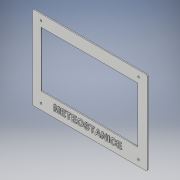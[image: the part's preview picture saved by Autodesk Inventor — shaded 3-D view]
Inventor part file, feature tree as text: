
AUTODESK INVENTOR PART (.ipt)
format: ipt  version: 2018 (Build 220112000, 112)  size: 400,384 bytes
history: native  units: in
note: dims shown in document units (in); Inventor stores cm internally (conversion verified against a paired STEP export)
features: extrude x2, sketch x2, fillet x1
ambient origin geometry x8: Origin, YZ Plane, XZ Plane, XY Plane, X Axis, Y Axis, Z Axis, Center Point
bodies: Solid1 (feature_tree)
feature tree (5):
  extrude  "Extrusion1"  Depth=5.2862in
  fillet  "Fillet1"  Radius=6.1417in
  extrude  "Extrusion2"  Depth=4.526in
  sketch  "Sketch1"  dims[d0=7.2795in d1=5.2862in d2=6.1417in]
  sketch  "Sketch2"  dims[d3=3.5039in d4=4.526in d5=0.1181in d6=6.1772in d7=0.3543in d8=0.063in d9=0.0in d10=0.0787in d11=0.0394in d12=0.0in d17=0.5906in d18=0.5472in]
